# Revit family: TYCO-FPP-Zettler-CIM800 contact input monitor module
name_source: partatom
category: Electrical Fixtures
revit_build: Autodesk Revit 2014 (Build: 20130308_1515(x64)
units: mm (PartAtom-declared; Revit-internal decimal feet)

## types (1)
- TYCO-FPP-Zettler-CIM800 contact input monitor module
    Alarm Resistance (s/c fault) = 100 Ohm
    Alarm State Current = 2.8mA
    Ambient Temperature = –25°C to +70°C
–25°C to +70°C
    Circuit Resistance = 10 Ohm
    Description = The CIM800 Addressable Contact Input Module supervises two
circuits of voltage-free contacts such as outputs from extinguishing
systems, ventilation controls, fire door controls, sprinkler flow
switches, non indicating detectors, etc.
    EOL Resistor = 200 Ohm
    Front Cover = Yes
    Length = 61 mm
    Loop Voltage = 20V to 40Vdc
    Manufacturer = Tyco
    Max. CIM800 per Loop2 = 200/250
    Model = Zettler-555.800.002
    PCB = PCB
    Quiescent Current = 275μA
    Rear Cover = Yes
    Relative Humidity = 10% to 95%
    Storage Temperature = –40°C to +80°C
    Type Comments = MX Addressable Module
    URL = https://www.tycosafetyproducts-anz.com
    Width = 84 mm
    Wire Size (maximum) = 2.5sq. mm

## geometry (parser evidence)
native form markers: Sweep x5
no freeform markers — native parametric forms only
